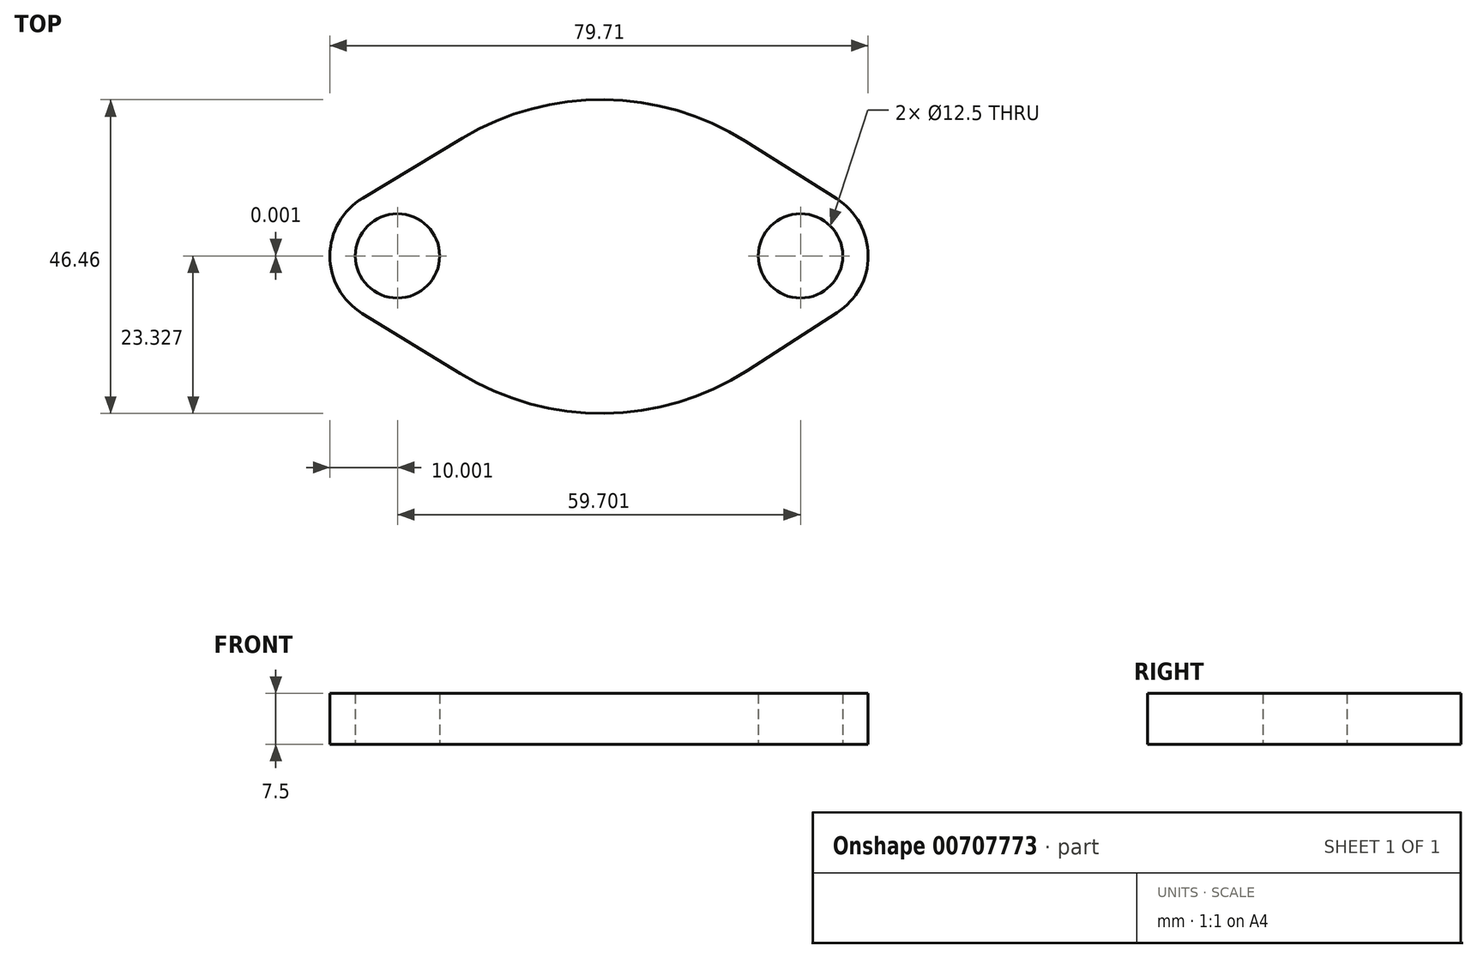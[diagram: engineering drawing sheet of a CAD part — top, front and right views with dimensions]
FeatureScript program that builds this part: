
annotation { "Feature Type Name" : "Feature", "Feature Type Description" : "" }
export const myFeature = defineFeature(function(context is Context, id is Id, definition is map)
    precondition{}
    {
        {
            var Q0;
            Q0=qCreatedBy(makeId("Top.planeOp"),FACE);
            var sketch = newSketch(context, id + "F0", { "sketchPlane" : qUnion([Q0])});
            skLineSegment(sketch, "E0", {"start": v(-35.95, -8.62) * mm, "end": v(-21.44, -17.52) * mm});
            skLineSegment(sketch, "E1", {"start": v(21.14, -17.05) * mm, "end": v(34.4, -8.5) * mm});
            skLineSegment(sketch, "E2", {"start": v(34.32, 8.37) * mm, "end": v(20.81, 16.88) * mm});
            skLineSegment(sketch, "E3", {"start": v(-21.1, 17.34) * mm, "end": v(-35.86, 8.48) * mm});
            skPoint(sketch, "E4.visualSharp", {"position": v(0, 30) * mm});
            skArc(sketch, "E4.filletArc", {"start": v(20.81, 16.88) * mm, "mid": v(-0.08, 23.04) * mm, "end": v(-21.1, 17.34) * mm});
            skPoint(sketch, "E5.visualSharp", {"position": v(-50, 0) * mm});
            skArc(sketch, "E5.filletArc", {"start": v(-35.86, 8.48) * mm, "mid": v(-40.72, -0.04) * mm, "end": v(-35.95, -8.62) * mm});
            skPoint(sketch, "E6.visualSharp", {"position": v(0, -30.66) * mm});
            skArc(sketch, "E6.filletArc", {"start": v(-21.44, -17.52) * mm, "mid": v(-0.08, -23.42) * mm, "end": v(21.14, -17.05) * mm});
            skPoint(sketch, "E7.visualSharp", {"position": v(47.6, 0) * mm});
            skArc(sketch, "E7.filletArc", {"start": v(34.4, -8.5) * mm, "mid": v(38.99, -0.04) * mm, "end": v(34.32, 8.37) * mm});
            skCircle(sketch, "E8", {"center": v(-30.72, -0.1) * mm, "radius": 6.25 * mm});
            skCircle(sketch, "E9", {"center": v(28.98, -0.1) * mm, "radius": 6.25 * mm});
            skSolve(sketch);
        }
        {
            var Q0;
            Q0=makeQuery(id+"F0.imprint","IMPRINT",FACE,{"disambiguationData":[TD([[makeQuery(id+"F0.imprint","IMPRINT",EDGE,{"derivedFrom":sQuery(id+"F0.wireOp",EDGE,"E0")}),1.0]])]});
            extrude(context, id + "F1", {"entities" : qUnion([Q0]), "depth" : 7.5 * mm, "offsetDistance" : 25.4 * mm});
        }
    });
